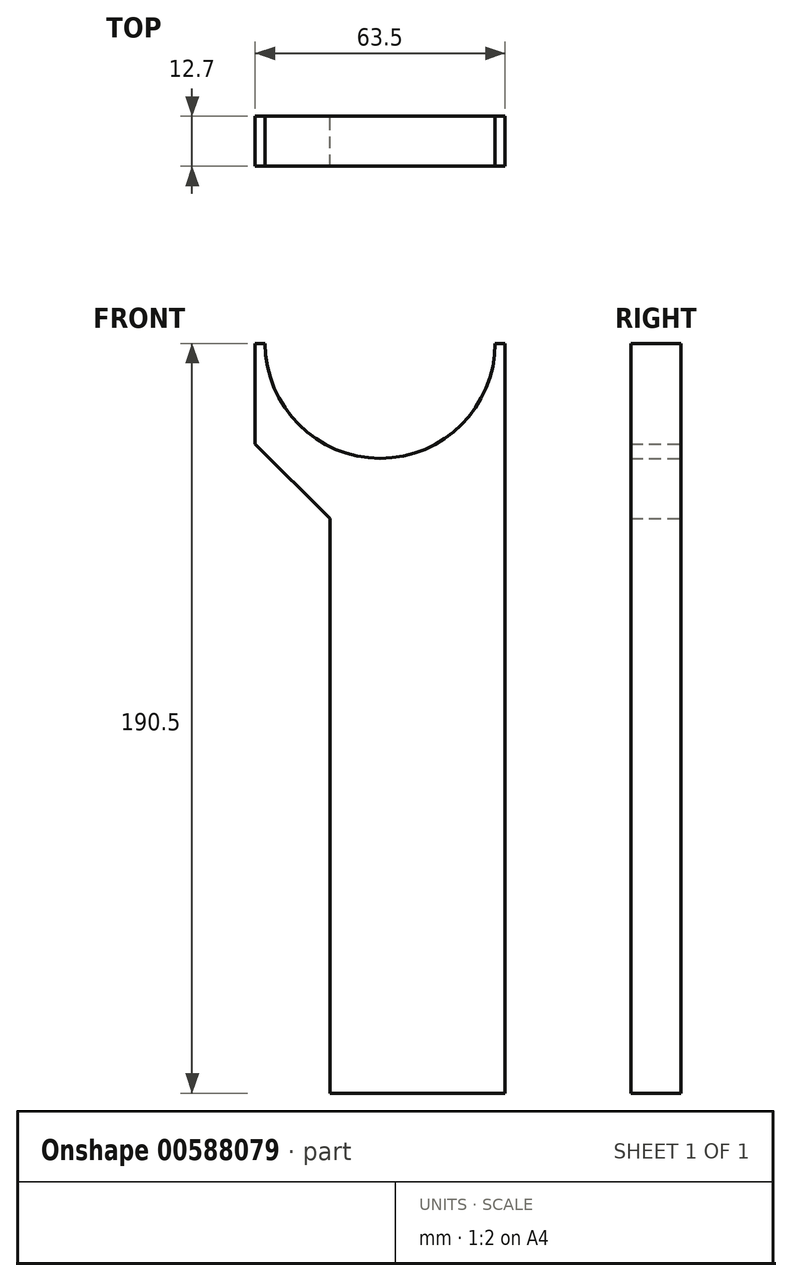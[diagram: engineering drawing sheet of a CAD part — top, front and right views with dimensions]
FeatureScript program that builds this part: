
annotation { "Feature Type Name" : "Feature", "Feature Type Description" : "" }
export const myFeature = defineFeature(function(context is Context, id is Id, definition is map)
    precondition{}
    {
        {
            var Q0;
            Q0=qCreatedBy(makeId("Front.planeOp"),FACE);
            var sketch = newSketch(context, id + "F0", { "sketchPlane" : qUnion([Q0])});
            skPoint(sketch, "E0.middle", {"position": v(0, 0) * mm});
            skArc(sketch, "E1", {"start": v(-27.16, 95.25) * mm, "mid": v(2.05, 66.04) * mm, "end": v(31.26, 95.25) * mm});
            skLineSegment(sketch, "E2", {"start": v(-27.16, 95.25) * mm, "end": v(-29.7, 95.25) * mm});
            skLineSegment(sketch, "E3", {"start": v(33.8, 0) * mm, "end": v(33.8, 95.25) * mm});
            skLineSegment(sketch, "E4", {"start": v(33.8, 95.25) * mm, "end": v(31.26, 95.25) * mm});
            skLineSegment(sketch, "E5", {"start": v(33.8, -95.25) * mm, "end": v(33.8, 0) * mm});
            skLineSegment(sketch, "E6", {"start": v(33.8, -95.25) * mm, "end": v(-10.65, -95.25) * mm});
            skLineSegment(sketch, "E7", {"start": v(-10.65, -95.25) * mm, "end": v(-10.65, 0) * mm});
            skLineSegment(sketch, "E8", {"start": v(-10.65, 0) * mm, "end": v(-10.65, 50.8) * mm});
            skLineSegment(sketch, "E9", {"start": v(-29.7, 69.64) * mm, "end": v(-29.7, 95.25) * mm});
            skLineSegment(sketch, "E10", {"start": v(-10.65, 50.8) * mm, "end": v(-29.7, 69.64) * mm});
            skPoint(sketch, "E11.orphan", {"position": v(-29.7, 50.8) * mm});
            skSolve(sketch);
        }
        {
            var Q0;
            Q0=makeQuery(id+"F0.imprint","IMPRINT",FACE,{"disambiguationData":[TD([[makeQuery(id+"F0.imprint","IMPRINT",EDGE,{"derivedFrom":sQuery(id+"F0.wireOp",EDGE,"E1")}),-1.0]])]});
            extrude(context, id + "F1", {"entities" : qUnion([Q0]), "depth" : 12.7 * mm, "offsetDistance" : 25.4 * mm});
        }
    });
